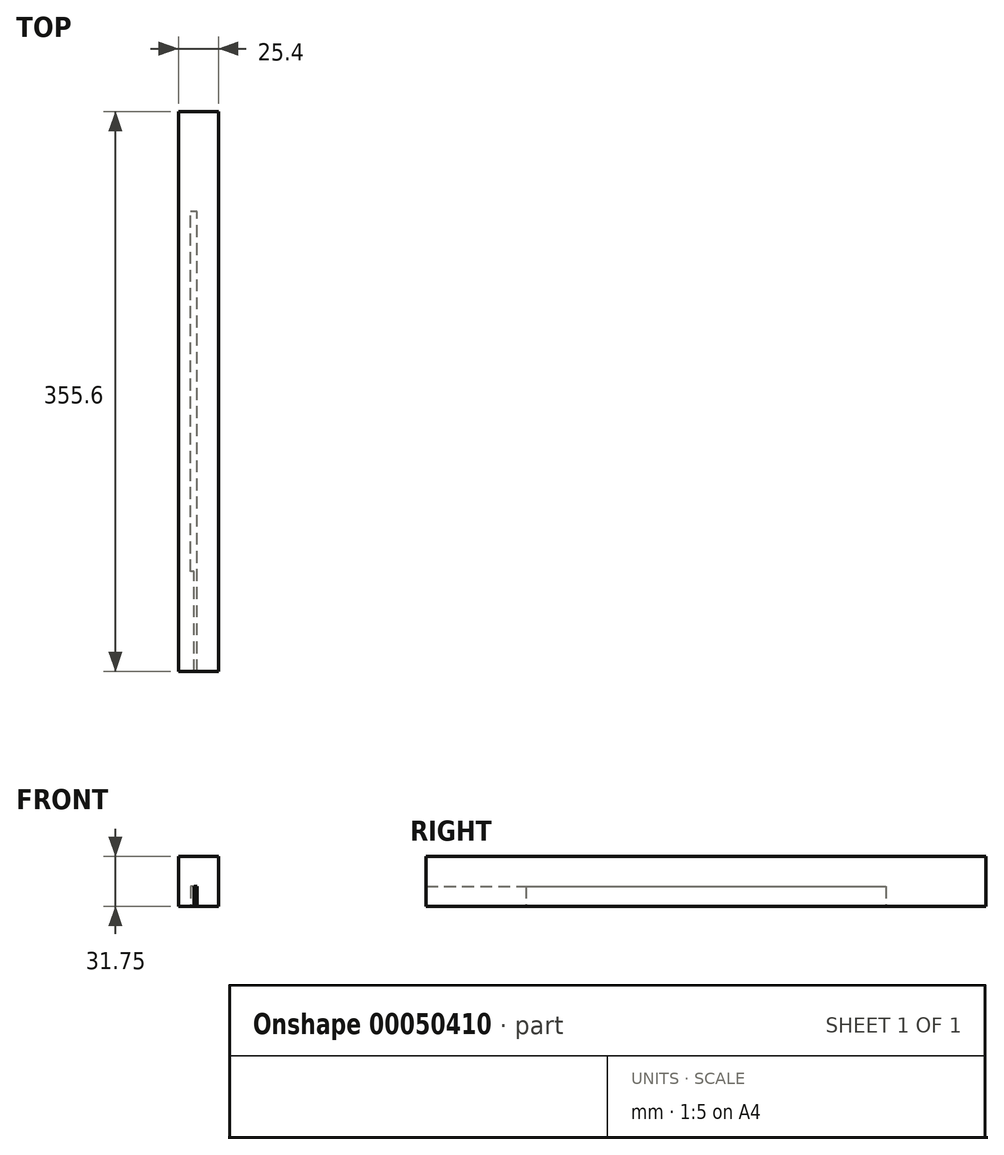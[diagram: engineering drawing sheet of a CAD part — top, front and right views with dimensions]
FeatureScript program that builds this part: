
annotation { "Feature Type Name" : "Feature", "Feature Type Description" : "" }
export const myFeature = defineFeature(function(context is Context, id is Id, definition is map)
    precondition{}
    {
        {
            var Q0;
            Q0=qCreatedBy(makeId("Right.planeOp"),FACE);
            var sketch = newSketch(context, id + "F0", { "sketchPlane" : qUnion([Q0])});
            skLineSegment(sketch, "E0.bottom", {"start": v(0, 0) * mm, "end": v(355.6, 0) * mm});
            skLineSegment(sketch, "E0.left", {"start": v(0, 0) * mm, "end": v(0, 19.45) * mm});
            skLineSegment(sketch, "E0.right", {"start": v(355.6, 0) * mm, "end": v(355.6, 19.45) * mm});
            skPoint(sketch, "E1", {"position": v(184.15, 76.2) * mm});
            skPoint(sketch, "E2", {"position": v(95.25, 57.15) * mm});
            skPoint(sketch, "E3", {"position": v(260.35, 57.15) * mm});
            skArc(sketch, "E4", {"start": v(260.35, 57.15) * mm, "mid": v(177.8, 76.3) * mm, "end": v(95.25, 57.15) * mm});
            skArc(sketch, "E5", {"start": v(11.9, 32.12) * mm, "mid": v(55.02, 39.83) * mm, "end": v(95.25, 57.15) * mm});
            skArc(sketch, "E6", {"start": v(260.35, 57.15) * mm, "mid": v(300.58, 39.83) * mm, "end": v(343.7, 32.12) * mm});
            skPoint(sketch, "E7.visualSharp", {"position": v(0, 31.75) * mm});
            skPoint(sketch, "E8.visualSharp", {"position": v(355.6, 31.75) * mm});
            skLineSegment(sketch, "E9", {"start": v(0, 19.45) * mm, "end": v(0, 31.75) * mm});
            skLineSegment(sketch, "E10", {"start": v(11.9, 32.12) * mm, "end": v(0, 31.75) * mm});
            skLineSegment(sketch, "E11", {"start": v(343.7, 32.12) * mm, "end": v(355.6, 31.75) * mm});
            skLineSegment(sketch, "E12", {"start": v(355.6, 19.45) * mm, "end": v(355.6, 31.75) * mm});
            skSolve(sketch);
        }
        {
            var Q0;
            Q0 = qSketchRegion(id + "F0", true);
            extrude(context, id + "F1", {"entities" : qUnion([Q0]), "depth" : 25.4 * mm});
        }
        {
            var Q0;
            Q0=makeQuery(id+"F1.opExtrude","SWEPT_FACE",FACE,{"disambiguationData":[OSD([sQuery(id+"F0.wireOp",EDGE,"E0.bottom")])]});
            var sketch = newSketch(context, id + "F2", { "sketchPlane" : qUnion([Q0])});
            skLineSegment(sketch, "E13.bottom", {"start": v(11.96, 0) * mm, "end": v(9.88, 0) * mm});
            skLineSegment(sketch, "E13.top", {"start": v(11.96, -63.5) * mm, "end": v(9.88, -63.5) * mm});
            skLineSegment(sketch, "E13.left", {"start": v(11.96, 0) * mm, "end": v(11.96, -63.5) * mm});
            skLineSegment(sketch, "E13.right", {"start": v(9.88, 0) * mm, "end": v(9.88, -63.5) * mm});
            skLineSegment(sketch, "E14.bottom", {"start": v(11.96, -63.5) * mm, "end": v(7.73, -63.5) * mm});
            skLineSegment(sketch, "E14.top", {"start": v(11.96, -292.1) * mm, "end": v(7.73, -292.1) * mm});
            skLineSegment(sketch, "E14.left", {"start": v(11.96, -63.5) * mm, "end": v(11.96, -292.1) * mm});
            skLineSegment(sketch, "E14.right", {"start": v(7.73, -63.5) * mm, "end": v(7.73, -292.1) * mm});
            skLineSegment(sketch, "E15.bottom", {"start": v(11.96, -292.1) * mm, "end": v(8.79, -292.1) * mm});
            skLineSegment(sketch, "E15.top", {"start": v(11.96, -355.6) * mm, "end": v(8.79, -355.6) * mm});
            skLineSegment(sketch, "E15.left", {"start": v(11.96, -292.1) * mm, "end": v(11.96, -355.6) * mm});
            skLineSegment(sketch, "E15.right", {"start": v(8.79, -292.1) * mm, "end": v(8.79, -355.6) * mm});
            skSolve(sketch);
        }
        {
            var Q0;
            Q0=makeQuery(id+"F2.imprint","IMPRINT",FACE,{"disambiguationData":[TD([[makeQuery(id+"F2.imprint","IMPRINT",EDGE,{"derivedFrom":sQuery(id+"F2.wireOp",EDGE,"E14.top")}),-1.0]])]});
            var Q1;
            Q1=makeQuery(id+"F2.imprint","IMPRINT",FACE,{"disambiguationData":[TD([[makeQuery(id+"F2.imprint","IMPRINT",EDGE,{"derivedFrom":sQuery(id+"F2.wireOp",EDGE,"E15.bottom")}),1.0]])]});
            var Q2;
            Q2=makeQuery(id+"F2.imprint","IMPRINT",FACE,{"disambiguationData":[TD([[makeQuery(id+"F2.imprint","IMPRINT",EDGE,{"derivedFrom":sQuery(id+"F2.wireOp",EDGE,"E13.bottom")}),1.0]])]});
            extrude(context, id + "F3", {"entities" : qUnion([Q0, Q1, Q2]), "operationType" : NewBodyOperationType.REMOVE, "oppositeDirection" : true, "depth" : 12.7 * mm});
        }
        {
            var Q0;
            Q0=makeQuery(id+"F1.opExtrude","CAP_FACE",FACE,{"disambiguationData":[OSD([sQuery(id+"F0.wireOp",EDGE,"E0.bottom"),sQuery(id+"F0.wireOp",EDGE,"E0.left"),sQuery(id+"F0.wireOp",EDGE,"E0.right"),sQuery(id+"F0.wireOp",EDGE,"E4"),sQuery(id+"F0.wireOp",EDGE,"E5"),sQuery(id+"F0.wireOp",EDGE,"E6"),sQuery(id+"F0.wireOp",EDGE,"E7.filletArc"),sQuery(id+"F0.wireOp",EDGE,"E8.filletArc")])],"isStart":false});
            var sketch = newSketch(context, id + "F4", { "sketchPlane" : qUnion([Q0])});
            skLineSegment(sketch, "E16.bottom", {"start": v(0, 0) * mm, "end": v(355.6, 0) * mm});
            skLineSegment(sketch, "E17.bottom", {"start": v(355.6, 31.75) * mm, "end": v(0, 31.75) * mm});
            skLineSegment(sketch, "E17.top", {"start": v(355.6, 90.35) * mm, "end": v(0, 90.35) * mm});
            skLineSegment(sketch, "E17.left", {"start": v(355.6, 31.75) * mm, "end": v(355.6, 90.35) * mm});
            skLineSegment(sketch, "E17.right", {"start": v(0, 31.75) * mm, "end": v(0, 90.35) * mm});
            skSolve(sketch);
        }
        {
            var Q0;
            Q0=makeQuery(id+"F4.imprint","IMPRINT",FACE,{"disambiguationData":[TD([[makeQuery(id+"F4.imprint","IMPRINT",EDGE,{"derivedFrom":sQuery(id+"F4.wireOp",EDGE,"E17.bottom")}),-1.0]])]});
            extrude(context, id + "F5", {"entities" : qUnion([Q0]), "operationType" : NewBodyOperationType.REMOVE, "oppositeDirection" : true, "depth" : 25.4 * mm});
        }
    });
